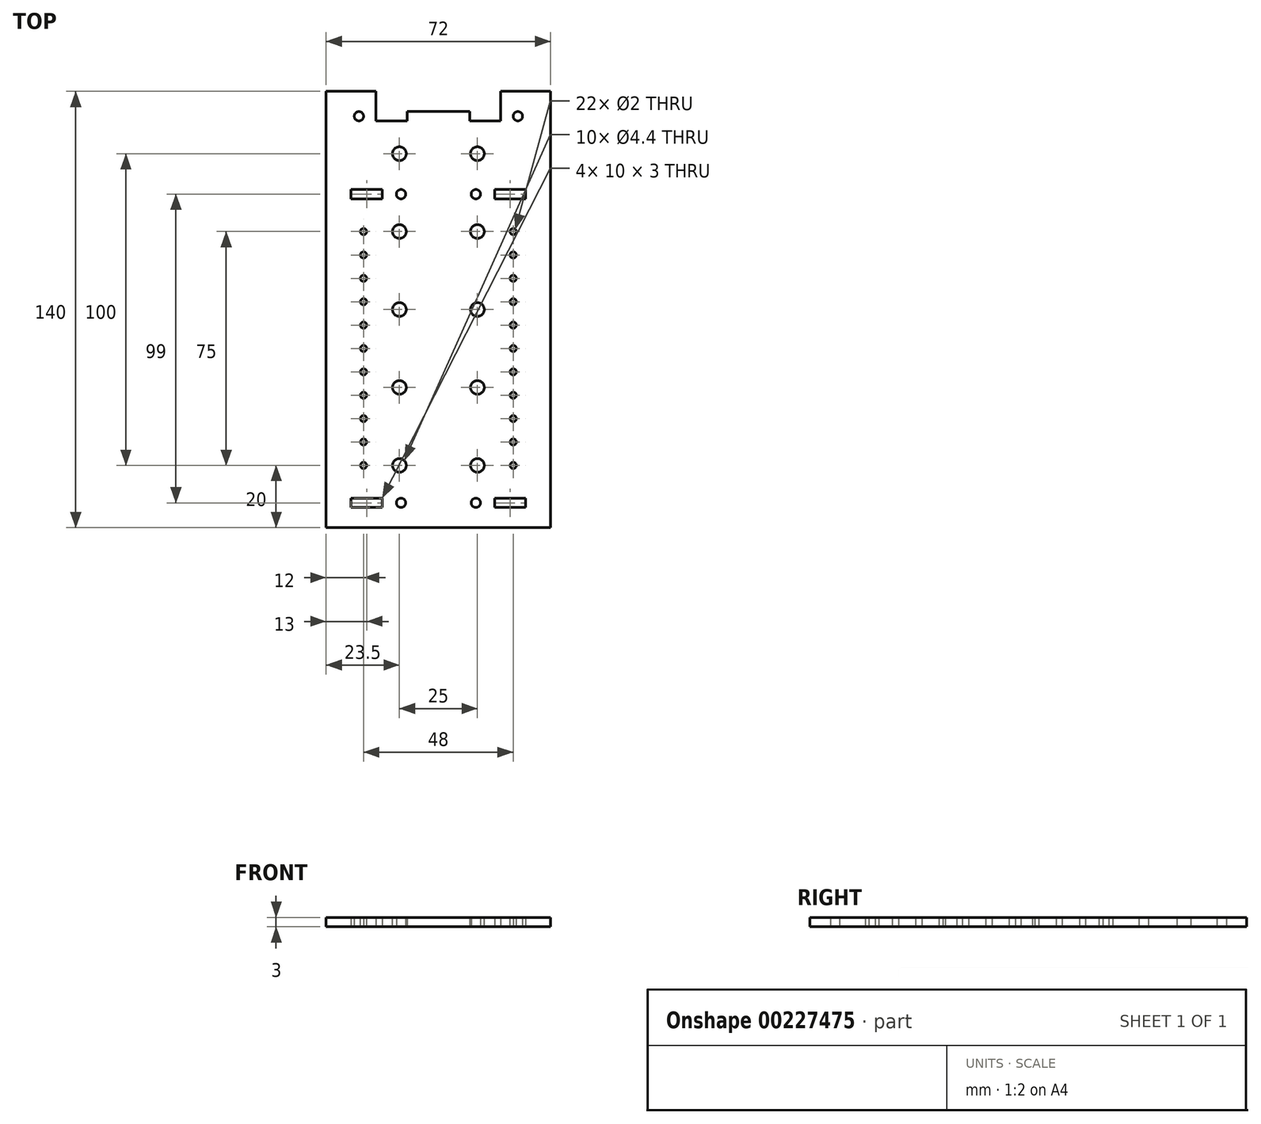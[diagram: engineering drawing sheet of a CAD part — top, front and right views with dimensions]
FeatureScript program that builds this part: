
annotation { "Feature Type Name" : "Feature", "Feature Type Description" : "" }
export const myFeature = defineFeature(function(context is Context, id is Id, definition is map)
    precondition{}
    {
        {
            assignVariable(context, id + "F0", {"name" : "Thickness", "anyValue" : 3});
        }
        {
            var Q0;
            Q0=qCreatedBy(makeId("Top.planeOp"),FACE);
            var sketch = newSketch(context, id + "F1", { "sketchPlane" : qUnion([Q0])});
            skLineSegment(sketch, "E0.bottom", {"start": v(36, -70) * mm, "end": v(-36, -70) * mm});
            skLineSegment(sketch, "E0.top", {"start": v(36, 70) * mm, "end": v(-36, 70) * mm});
            skLineSegment(sketch, "E0.left", {"start": v(36, -70) * mm, "end": v(36, 70) * mm});
            skLineSegment(sketch, "E0.right", {"start": v(-36, -70) * mm, "end": v(-36, 70) * mm});
            skPoint(sketch, "E0.middle", {"position": v(0, 0) * mm});
            skLineSegment(sketch, "E1", {"start": v(-36, 62) * mm, "end": v(36, 62) * mm, "construction": true});
            skPoint(sketch, "E2", {"position": v(-15, 62) * mm});
            skLineSegment(sketch, "E3.bottom", {"start": v(-10, 60.5) * mm, "end": v(-20, 60.5) * mm});
            skLineSegment(sketch, "E3.top", {"start": v(-10, 63.5) * mm, "end": v(-20, 63.5) * mm});
            skLineSegment(sketch, "E3.left", {"start": v(-10, 60.5) * mm, "end": v(-10, 63.5) * mm});
            skLineSegment(sketch, "E3.right", {"start": v(-20, 60.5) * mm, "end": v(-20, 63.5) * mm});
            skLineSegment(sketch, "E4.MirrorCS", {"start": v(10, 60.5) * mm, "end": v(10, 63.5) * mm});
            skLineSegment(sketch, "E5.MirrorCS", {"start": v(10, 63.5) * mm, "end": v(20, 63.5) * mm});
            skLineSegment(sketch, "E6.MirrorCS", {"start": v(20, 60.5) * mm, "end": v(20, 63.5) * mm});
            skLineSegment(sketch, "E7.MirrorCS", {"start": v(10, 60.5) * mm, "end": v(20, 60.5) * mm});
            skLineSegment(sketch, "E8.MirrorCS", {"start": v(-36, -62) * mm, "end": v(36, -62) * mm, "construction": true});
            skLineSegment(sketch, "E9", {"start": v(-36, 49.5) * mm, "end": v(36, 49.5) * mm, "construction": true});
            skLineSegment(sketch, "E10.MirrorCS", {"start": v(-36, 37) * mm, "end": v(36, 37) * mm, "construction": true});
            skLineSegment(sketch, "E11", {"start": v(-20, 63.5) * mm, "end": v(-20, 70) * mm});
            skLineSegment(sketch, "E12.MirrorCS", {"start": v(20, 63.5) * mm, "end": v(20, 70) * mm});
            skLineSegment(sketch, "E13", {"start": v(-10, 63.5) * mm, "end": v(10, 63.5) * mm});
            skLineSegment(sketch, "E14.bottom", {"start": v(-18, -63.5) * mm, "end": v(-28, -63.5) * mm});
            skLineSegment(sketch, "E14.top", {"start": v(-18, -60.5) * mm, "end": v(-28, -60.5) * mm});
            skLineSegment(sketch, "E14.left", {"start": v(-18, -63.5) * mm, "end": v(-18, -60.5) * mm});
            skLineSegment(sketch, "E14.right", {"start": v(-28, -63.5) * mm, "end": v(-28, -60.5) * mm});
            skPoint(sketch, "E14.middle", {"position": v(-23, -62) * mm});
            skLineSegment(sketch, "E15.MirrorCS", {"start": v(18, -63.5) * mm, "end": v(28, -63.5) * mm});
            skLineSegment(sketch, "E16.MirrorCS", {"start": v(18, -63.5) * mm, "end": v(18, -60.5) * mm});
            skLineSegment(sketch, "E17.MirrorCS", {"start": v(18, -60.5) * mm, "end": v(28, -60.5) * mm});
            skPoint(sketch, "E18.MirrorP", {"position": v(23, -62) * mm});
            skLineSegment(sketch, "E19.MirrorCS", {"start": v(28, -63.5) * mm, "end": v(28, -60.5) * mm});
            skLineSegment(sketch, "E20.bottom", {"start": v(-18, 35.5) * mm, "end": v(-28, 35.5) * mm});
            skLineSegment(sketch, "E20.top", {"start": v(-18, 38.5) * mm, "end": v(-28, 38.5) * mm});
            skLineSegment(sketch, "E20.left", {"start": v(-18, 35.5) * mm, "end": v(-18, 38.5) * mm});
            skLineSegment(sketch, "E20.right", {"start": v(-28, 35.5) * mm, "end": v(-28, 38.5) * mm});
            skPoint(sketch, "E20.middle", {"position": v(-23, 37) * mm});
            skPoint(sketch, "E21.MirrorP", {"position": v(23, 37) * mm});
            skLineSegment(sketch, "E22.MirrorCS", {"start": v(28, 35.5) * mm, "end": v(28, 38.5) * mm});
            skLineSegment(sketch, "E23.MirrorCS", {"start": v(18, 35.5) * mm, "end": v(28, 35.5) * mm});
            skLineSegment(sketch, "E24.MirrorCS", {"start": v(18, 35.5) * mm, "end": v(18, 38.5) * mm});
            skLineSegment(sketch, "E25.MirrorCS", {"start": v(18, 38.5) * mm, "end": v(28, 38.5) * mm});
            skSolve(sketch);
        }
        {
            var Q0;
            Q0=makeQuery(id+"F1.imprint","IMPRINT",FACE,{"disambiguationData":[TD([[makeQuery(id+"F1.imprint","IMPRINT",EDGE,{"derivedFrom":sQuery(id+"F1.wireOp",EDGE,"E0.bottom")}),-1.0]])]});
            extrude(context, id + "F2", {"entities" : qUnion([Q0]), "depth" : (getVariable(context, 'Thickness')) * mm});
        }
        {
            var Q0;
            Q0=makeQuery(id+"F2.opExtrude","CAP_FACE",FACE,{"disambiguationData":[OSD([sQuery(id+"F1.wireOp",EDGE,"E0.bottom"),sQuery(id+"F1.wireOp",EDGE,"E0.top"),sQuery(id+"F1.wireOp",EDGE,"E0.left"),sQuery(id+"F1.wireOp",EDGE,"E0.right")])],"isStart":false});
            var sketch = newSketch(context, id + "F3", { "sketchPlane" : qUnion([Q0])});
            skPoint(sketch, "E26", {"position": v(-24, -50) * mm});
            skPoint(sketch, "E27.0.1.0", {"position": v(-24, -42.5) * mm});
            skPoint(sketch, "E27.0.2.0", {"position": v(-24, -35) * mm});
            skPoint(sketch, "E27.1.0.0", {"position": v(24, -50) * mm});
            skPoint(sketch, "E27.1.1.0", {"position": v(24, -42.5) * mm});
            skPoint(sketch, "E27.1.2.0", {"position": v(24, -35) * mm});
            skLineSegment(sketch, "E27.direction1", {"start": v(-24, -50) * mm, "end": v(24, -50) * mm, "construction": true});
            skLineSegment(sketch, "E27.direction2", {"start": v(-24, -50) * mm, "end": v(-24, -42.5) * mm, "construction": true});
            skPoint(sketch, "E28.0.0.3", {"position": v(-24, -27.5) * mm});
            skPoint(sketch, "E28.0.1.3", {"position": v(24, -27.5) * mm});
            skPoint(sketch, "E29.0.0.4", {"position": v(-24, -20) * mm});
            skPoint(sketch, "E29.0.1.4", {"position": v(24, -20) * mm});
            skPoint(sketch, "E30.0.0.5", {"position": v(-24, -12.5) * mm});
            skPoint(sketch, "E30.0.0.6", {"position": v(-24, -5) * mm});
            skPoint(sketch, "E30.0.0.7", {"position": v(-24, 2.5) * mm});
            skPoint(sketch, "E30.0.0.8", {"position": v(-24, 10) * mm});
            skPoint(sketch, "E30.0.0.9", {"position": v(-24, 17.5) * mm});
            skPoint(sketch, "E30.0.1.5", {"position": v(24, -12.5) * mm});
            skPoint(sketch, "E30.0.1.6", {"position": v(24, -5) * mm});
            skPoint(sketch, "E30.0.1.7", {"position": v(24, 2.5) * mm});
            skPoint(sketch, "E30.0.1.8", {"position": v(24, 10) * mm});
            skPoint(sketch, "E30.0.1.9", {"position": v(24, 17.5) * mm});
            skPoint(sketch, "E31.0.0.10", {"position": v(-24, 25) * mm});
            skPoint(sketch, "E31.0.1.10", {"position": v(24, 25) * mm});
            skSolve(sketch);
        }
        {
            var Q0;
            Q0=sQuery(id+"F3.wireOp",VERTEX,"E27.1.0.0");
            var Q1;
            Q1=sQuery(id+"F3.wireOp",VERTEX,"E27.1.1.0");
            var Q2;
            Q2=sQuery(id+"F3.wireOp",VERTEX,"E27.1.2.0");
            var Q3;
            Q3=sQuery(id+"F3.wireOp",VERTEX,"E26");
            var Q4;
            Q4=sQuery(id+"F3.wireOp",VERTEX,"E27.0.1.0");
            var Q5;
            Q5=sQuery(id+"F3.wireOp",VERTEX,"E27.0.2.0");
            var Q6;
            Q6=sQuery(id+"F3.wireOp",VERTEX,"E28.0.0.3");
            var Q7;
            Q7=sQuery(id+"F3.wireOp",VERTEX,"E28.0.1.3");
            var Q8;
            Q8=sQuery(id+"F3.wireOp",VERTEX,"E29.0.0.4");
            var Q9;
            Q9=sQuery(id+"F3.wireOp",VERTEX,"E29.0.1.4");
            var Q10;
            Q10=sQuery(id+"F3.wireOp",VERTEX,"E29.0.0.5");
            var Q11;
            Q11=sQuery(id+"F3.wireOp",VERTEX,"E29.0.1.5");
            var Q12;
            Q12=sQuery(id+"F3.wireOp",VERTEX,"E29.0.0.6");
            var Q13;
            Q13=sQuery(id+"F3.wireOp",VERTEX,"E29.0.1.6");
            var Q14;
            Q14=sQuery(id+"F3.wireOp",VERTEX,"E29.0.0.7");
            var Q15;
            Q15=sQuery(id+"F3.wireOp",VERTEX,"E29.0.1.7");
            var Q16;
            Q16=sQuery(id+"F3.wireOp",VERTEX,"E30.0.0.5");
            var Q17;
            Q17=sQuery(id+"F3.wireOp",VERTEX,"E30.0.0.6");
            var Q18;
            Q18=sQuery(id+"F3.wireOp",VERTEX,"E30.0.0.7");
            var Q19;
            Q19=sQuery(id+"F3.wireOp",VERTEX,"E30.0.0.8");
            var Q20;
            Q20=sQuery(id+"F3.wireOp",VERTEX,"E30.0.0.9");
            var Q21;
            Q21=sQuery(id+"F3.wireOp",VERTEX,"E30.0.1.5");
            var Q22;
            Q22=sQuery(id+"F3.wireOp",VERTEX,"E30.0.1.6");
            var Q23;
            Q23=sQuery(id+"F3.wireOp",VERTEX,"E30.0.1.7");
            var Q24;
            Q24=sQuery(id+"F3.wireOp",VERTEX,"E30.0.1.8");
            var Q25;
            Q25=sQuery(id+"F3.wireOp",VERTEX,"E30.0.1.9");
            var Q26;
            Q26=sQuery(id+"F3.wireOp",VERTEX,"E31.0.0.10");
            var Q27;
            Q27=sQuery(id+"F3.wireOp",VERTEX,"E31.0.1.10");
            var Q28;
            Q28=makeQuery(id+"F2.opExtrude","SWEPT_BODY",BODY,{"disambiguationData":[OSD([sQuery(id+"F1.wireOp",EDGE,"E0.bottom"),sQuery(id+"F1.wireOp",EDGE,"E0.top"),sQuery(id+"F1.wireOp",EDGE,"E0.left"),sQuery(id+"F1.wireOp",EDGE,"E0.right")])]});
            hole(context, id + "F4", {"style" : HoleStyle.SIMPLE, "endStyle" : HoleEndStyle.THROUGH, "holeDiameter" : 2 * mm, "locations" : qUnion([Q0, Q1, Q2, Q3, Q4, Q5, Q6, Q7, Q8, Q9, Q10, Q11, Q12, Q13, Q14, Q15, Q16, Q17, Q18, Q19, Q20, Q21, Q22, Q23, Q24, Q25, Q26, Q27]), "scope" : qUnion([Q28]), "tappedDepth" : 12 * mm, "tapClearance" : 3, "majorDiameter" : 5 * mm});
        }
        {
            var Q0;
            Q0=makeQuery(id+"F2.opExtrude","CAP_FACE",FACE,{"disambiguationData":[OSD([sQuery(id+"F1.wireOp",EDGE,"E0.bottom"),sQuery(id+"F1.wireOp",EDGE,"E0.top"),sQuery(id+"F1.wireOp",EDGE,"E0.left"),sQuery(id+"F1.wireOp",EDGE,"E0.right")])],"isStart":true});
            var sketch = newSketch(context, id + "F5", { "sketchPlane" : qUnion([Q0])});
            skPoint(sketch, "E32", {"position": v(-25.5, -62) * mm});
            skPoint(sketch, "E33.MirrorP", {"position": v(25.5, -62) * mm});
            skPoint(sketch, "E34", {"position": v(-12, 62) * mm});
            skPoint(sketch, "E34.positionSnap0", {"position": v(-18, 62) * mm});
            skPoint(sketch, "E35.MirrorP", {"position": v(12, 62) * mm});
            skPoint(sketch, "E36", {"position": v(-12, -37) * mm});
            skPoint(sketch, "E36.positionSnap0", {"position": v(-18, -37) * mm});
            skPoint(sketch, "E37.MirrorP", {"position": v(12, -37) * mm});
            skSolve(sketch);
        }
        {
            var Q0;
            Q0=sQuery(id+"F5.wireOp",VERTEX,"E32");
            var Q1;
            Q1=sQuery(id+"F5.wireOp",VERTEX,"E33.MirrorP");
            var Q2;
            Q2=sQuery(id+"F5.wireOp",VERTEX,"c4c34262-3dce-454e-b2bd-f3ae62b3c4420.MirrorP");
            var Q3;
            Q3=sQuery(id+"F5.wireOp",VERTEX,"0a803537-de52-45db-abf5-6d0ac05b4b1c0.MirrorP");
            var Q4;
            Q4=sQuery(id+"F5.wireOp",VERTEX,"dc16f88a-1483-4052-b3e8-af829b696ef1");
            var Q5;
            Q5=sQuery(id+"F5.wireOp",VERTEX,"47d0393d-9516-4e0f-91cd-c7c6b75bc53c0.MirrorP");
            var Q6;
            Q6=sQuery(id+"F5.wireOp",VERTEX,"E34");
            var Q7;
            Q7=sQuery(id+"F5.wireOp",VERTEX,"E35.MirrorP");
            var Q8;
            Q8=sQuery(id+"F5.wireOp",VERTEX,"E36");
            var Q9;
            Q9=sQuery(id+"F5.wireOp",VERTEX,"E37.MirrorP");
            var Q10;
            Q10=makeQuery(id+"F2.opExtrude","SWEPT_BODY",BODY,{"disambiguationData":[OSD([sQuery(id+"F1.wireOp",EDGE,"E0.bottom"),sQuery(id+"F1.wireOp",EDGE,"E0.top"),sQuery(id+"F1.wireOp",EDGE,"E0.left"),sQuery(id+"F1.wireOp",EDGE,"E0.right")])]});
            hole(context, id + "F6", {"style" : HoleStyle.SIMPLE, "endStyle" : HoleEndStyle.THROUGH, "holeDiameter" : 3 * mm, "locations" : qUnion([Q0, Q1, Q2, Q3, Q4, Q5, Q6, Q7, Q8, Q9]), "scope" : qUnion([Q10]), "tappedDepth" : 12 * mm, "tapClearance" : 3});
        }
        {
            var Q0;
            Q0=makeQuery(id+"F2.opExtrude","CAP_FACE",FACE,{"disambiguationData":[OSD([sQuery(id+"F1.wireOp",EDGE,"E0.bottom"),sQuery(id+"F1.wireOp",EDGE,"E0.top"),sQuery(id+"F1.wireOp",EDGE,"E0.left"),sQuery(id+"F1.wireOp",EDGE,"E0.right")])],"isStart":false});
            var sketch = newSketch(context, id + "F7", { "sketchPlane" : qUnion([Q0])});
            skPoint(sketch, "E38", {"position": v(-12.5, -50) * mm});
            skPoint(sketch, "E39.0.1.0", {"position": v(-12.5, -25) * mm});
            skPoint(sketch, "E39.1.0.0", {"position": v(12.5, -50) * mm});
            skPoint(sketch, "E39.1.1.0", {"position": v(12.5, -25) * mm});
            skLineSegment(sketch, "E39.direction1", {"start": v(-12.5, -50) * mm, "end": v(12.5, -50) * mm, "construction": true});
            skLineSegment(sketch, "E39.direction2", {"start": v(-12.5, -50) * mm, "end": v(-12.5, -25) * mm, "construction": true});
            skPoint(sketch, "E40.0.0.2", {"position": v(-12.5, 0) * mm});
            skPoint(sketch, "E40.0.1.2", {"position": v(12.5, 0) * mm});
            skPoint(sketch, "E41.0.0.3", {"position": v(-12.5, 25) * mm});
            skPoint(sketch, "E41.0.0.4", {"position": v(-12.5, 50) * mm});
            skPoint(sketch, "E41.0.1.3", {"position": v(12.5, 25) * mm});
            skPoint(sketch, "E41.0.1.4", {"position": v(12.5, 50) * mm});
            skSolve(sketch);
        }
        {
            var Q0;
            Q0=sQuery(id+"F7.wireOp",VERTEX,"E38");
            var Q1;
            Q1=sQuery(id+"F7.wireOp",VERTEX,"E39.1.0.0");
            var Q2;
            Q2=sQuery(id+"F7.wireOp",VERTEX,"E39.2.0.0");
            var Q3;
            Q3=sQuery(id+"F7.wireOp",VERTEX,"E39.0.1.0");
            var Q4;
            Q4=sQuery(id+"F7.wireOp",VERTEX,"E39.1.1.0");
            var Q5;
            Q5=sQuery(id+"F7.wireOp",VERTEX,"E39.2.1.0");
            var Q6;
            Q6=sQuery(id+"F7.wireOp",VERTEX,"E39.0.2.0");
            var Q7;
            Q7=sQuery(id+"F7.wireOp",VERTEX,"E39.1.2.0");
            var Q8;
            Q8=sQuery(id+"F7.wireOp",VERTEX,"E39.2.2.0");
            var Q9;
            Q9=sQuery(id+"F7.wireOp",VERTEX,"E40.0.0.2");
            var Q10;
            Q10=sQuery(id+"F7.wireOp",VERTEX,"E40.0.1.2");
            var Q11;
            Q11=sQuery(id+"F7.wireOp",VERTEX,"ea0734de-f32a-4cc6-85a0-2a80a2044444.0.0.3");
            var Q12;
            Q12=sQuery(id+"F7.wireOp",VERTEX,"ea0734de-f32a-4cc6-85a0-2a80a2044444.0.1.3");
            var Q13;
            Q13=sQuery(id+"F7.wireOp",VERTEX,"ea0734de-f32a-4cc6-85a0-2a80a2044444.0.0.4");
            var Q14;
            Q14=sQuery(id+"F7.wireOp",VERTEX,"ea0734de-f32a-4cc6-85a0-2a80a2044444.0.1.4");
            var Q15;
            Q15=sQuery(id+"F7.wireOp",VERTEX,"E41.0.0.3");
            var Q16;
            Q16=sQuery(id+"F7.wireOp",VERTEX,"E41.0.1.3");
            var Q17;
            Q17=sQuery(id+"F7.wireOp",VERTEX,"E41.0.0.4");
            var Q18;
            Q18=sQuery(id+"F7.wireOp",VERTEX,"E41.0.1.4");
            var Q19;
            Q19=makeQuery(id+"F2.opExtrude","SWEPT_BODY",BODY,{"disambiguationData":[OSD([sQuery(id+"F1.wireOp",EDGE,"E0.bottom"),sQuery(id+"F1.wireOp",EDGE,"E0.top"),sQuery(id+"F1.wireOp",EDGE,"E0.left"),sQuery(id+"F1.wireOp",EDGE,"E0.right")])]});
            hole(context, id + "F8", {"style" : HoleStyle.SIMPLE, "endStyle" : HoleEndStyle.THROUGH, "standardTappedOrClearance" : lookupTablePath({ "standard" : "ISO", "fit" : "Normal", "size" : "M4", "type" : "Clearance" }), "standardBlindInLast" : lookupTablePath({ "fit" : "Standard", "standard" : "ISO", "size" : "M4", "type" : "Clearance" }), "holeDiameter" : 4.4 * mm, "locations" : qUnion([Q0, Q1, Q2, Q3, Q4, Q5, Q6, Q7, Q8, Q9, Q10, Q11, Q12, Q13, Q14, Q15, Q16, Q17, Q18]), "scope" : qUnion([Q19]), "tappedDepth" : 12 * mm, "tapClearance" : 3});
        }
    });
